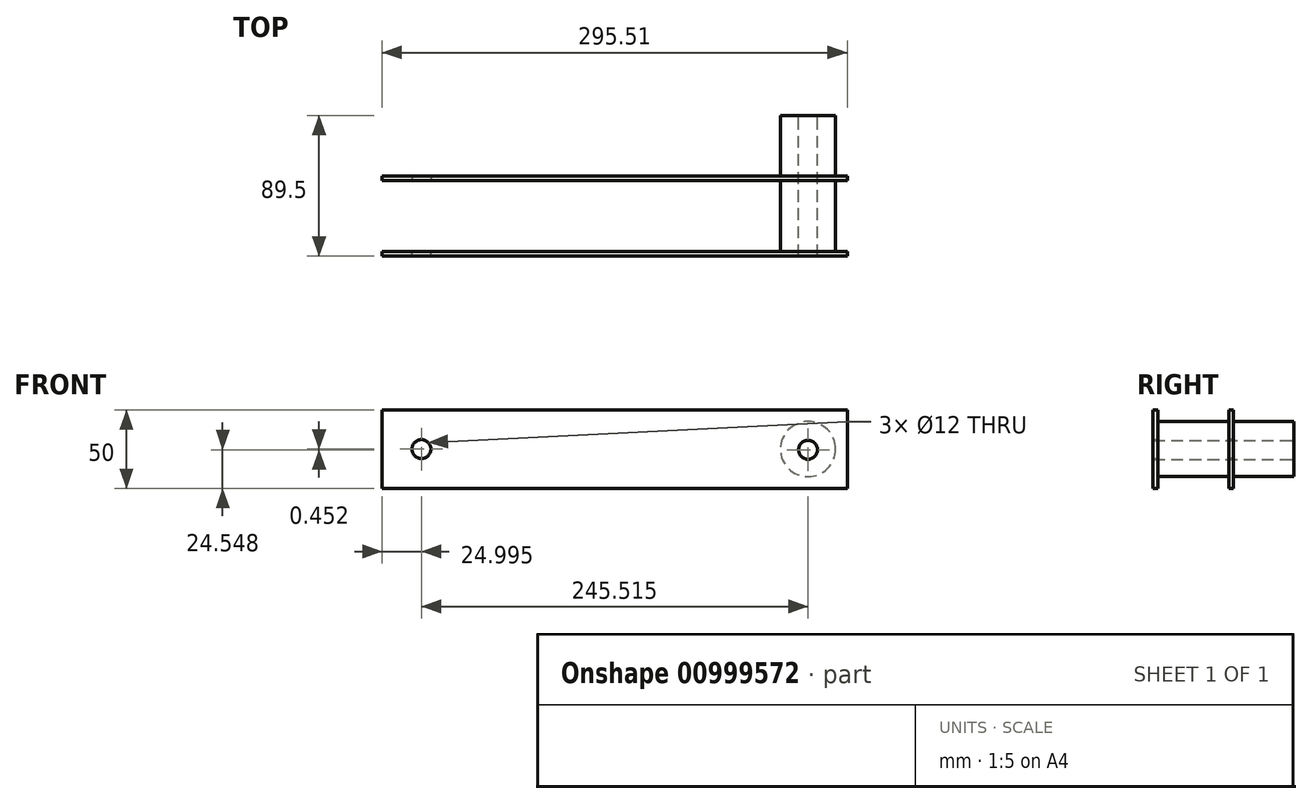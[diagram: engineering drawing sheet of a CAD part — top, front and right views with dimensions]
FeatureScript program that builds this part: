
annotation { "Feature Type Name" : "Feature", "Feature Type Description" : "" }
export const myFeature = defineFeature(function(context is Context, id is Id, definition is map)
    precondition{}
    {
        {
            var Q0;
            Q0=qCreatedBy(makeId("Front.planeOp"),FACE);
            var sketch = newSketch(context, id + "F0", { "sketchPlane" : qUnion([Q0])});
            skCircle(sketch, "E0", {"center": v(0, 0) * mm, "radius": 17.5 * mm});
            skSolve(sketch);
        }
        {
            var Q0;
            Q0=makeQuery(id+"F0.imprint","IMPRINT",FACE,{"disambiguationData":[TD([[makeQuery(id+"F0.imprint","IMPRINT",EDGE,{"derivedFrom":sQuery(id+"F0.wireOp",EDGE,"E0")}),1.0]])]});
            extrude(context, id + "F1", {"entities" : qUnion([Q0]), "depth" : 41.5 * mm, "offsetDistance" : 25 * mm});
        }
        {
            var Q0;
            Q0=makeQuery(id+"F1.opExtrude","CAP_FACE",FACE,{"disambiguationData":[OSD([sQuery(id+"F0.wireOp",EDGE,"E0")])],"isStart":false});
            var sketch = newSketch(context, id + "F2", { "sketchPlane" : qUnion([Q0])});
            skLineSegment(sketch, "E1", {"start": v(0, 0) * mm, "end": v(-245.51, 0) * mm, "construction": true});
            skLineSegment(sketch, "E2.bottom", {"start": v(25, -25) * mm, "end": v(-270.51, -25) * mm});
            skLineSegment(sketch, "E2.top", {"start": v(25, 25) * mm, "end": v(-270.51, 25) * mm});
            skLineSegment(sketch, "E2.left", {"start": v(25, -25) * mm, "end": v(25, 25) * mm});
            skLineSegment(sketch, "E2.right", {"start": v(-270.51, -25) * mm, "end": v(-270.51, 25) * mm});
            skPoint(sketch, "E2.middle", {"position": v(-122.76, 0) * mm});
            skCircle(sketch, "E3", {"center": v(-245.51, 0) * mm, "radius": 6 * mm});
            skSolve(sketch);
        }
        {
            var Q0;
            Q0 = qSketchRegion(id + "F2", true);
            extrude(context, id + "F3", {"entities" : qUnion([Q0]), "operationType" : NewBodyOperationType.ADD, "oppositeDirection" : true, "depth" : 3 * mm, "offsetDistance" : 25 * mm});
        }
        {
            var Q0;
            Q0=makeQuery(id+"F3.boolean.opBoolean","MERGE",FACE,{"derivedFrom":[makeQuery(id+"F1.opExtrude","CAP_FACE",FACE,{"disambiguationData":[OSD([sQuery(id+"F0.wireOp",EDGE,"E0")])],"isStart":false}),makeQuery(id+"F3.opExtrude","CAP_FACE",FACE,{"disambiguationData":[OSD([sQuery(id+"F2.wireOp",EDGE,"E2.bottom"),sQuery(id+"F2.wireOp",EDGE,"E2.top"),sQuery(id+"F2.wireOp",EDGE,"E2.left"),sQuery(id+"F2.wireOp",EDGE,"E2.right")])],"isStart":true})]});
            var sketch = newSketch(context, id + "F4", { "sketchPlane" : qUnion([Q0])});
            skCircle(sketch, "E4", {"center": v(0, 0) * mm, "radius": 17.5 * mm});
            skSolve(sketch);
        }
        {
            var Q0;
            Q0=makeQuery(id+"F4.imprint","IMPRINT",FACE,{"disambiguationData":[TD([[makeQuery(id+"F4.imprint","IMPRINT",EDGE,{"derivedFrom":sQuery(id+"F4.wireOp",EDGE,"E4")}),1.0]])]});
            extrude(context, id + "F5", {"entities" : qUnion([Q0]), "operationType" : NewBodyOperationType.ADD, "depth" : 45 * mm, "offsetDistance" : 25 * mm});
        }
        {
            var Q0;
            Q0=makeQuery(id+"F5.opExtrude","CAP_FACE",FACE,{"disambiguationData":[OSD([sQuery(id+"F4.wireOp",EDGE,"E4")])],"isStart":false});
            var sketch = newSketch(context, id + "F6", { "sketchPlane" : qUnion([Q0])});
            skLineSegment(sketch, "E5.bottom", {"start": v(-270.51, 25) * mm, "end": v(25, 25) * mm});
            skLineSegment(sketch, "E5.top", {"start": v(-270.51, -25) * mm, "end": v(25, -25) * mm});
            skLineSegment(sketch, "E5.left", {"start": v(-270.51, 25) * mm, "end": v(-270.51, -25) * mm});
            skLineSegment(sketch, "E5.right", {"start": v(25, 25) * mm, "end": v(25, -25) * mm});
            skCircle(sketch, "E6", {"center": v(-245.51, 0) * mm, "radius": 6 * mm});
            skSolve(sketch);
        }
        {
            var Q0;
            Q0 = qSketchRegion(id + "F6", true);
            extrude(context, id + "F7", {"entities" : qUnion([Q0]), "operationType" : NewBodyOperationType.ADD, "depth" : 3 * mm, "offsetDistance" : 25 * mm});
        }
        {
            var Q0;
            Q0=qCreatedBy(makeId("Front.planeOp"),FACE);
            var sketch = newSketch(context, id + "F8", { "sketchPlane" : qUnion([Q0])});
            skCircle(sketch, "E7", {"center": v(0, -0.45) * mm, "radius": 6 * mm});
            skSolve(sketch);
        }
        {
            var Q0;
            Q0 = qSketchRegion(id + "F8", true);
            extrude(context, id + "F9", {"entities" : qUnion([Q0]), "operationType" : NewBodyOperationType.REMOVE, "endBound" : BoundingType.THROUGH_ALL, "depth" : 25 * mm, "offsetDistance" : 25 * mm});
        }
    });
